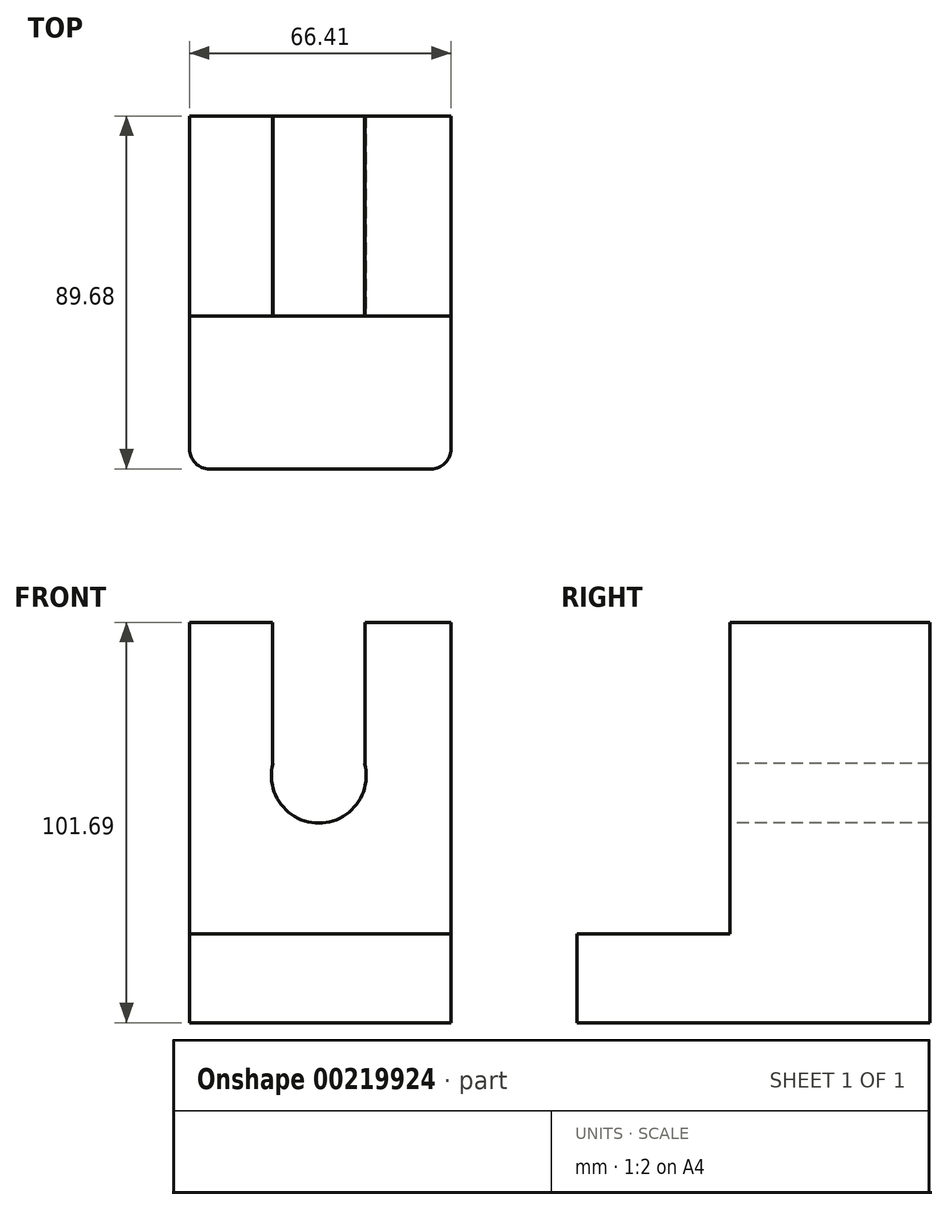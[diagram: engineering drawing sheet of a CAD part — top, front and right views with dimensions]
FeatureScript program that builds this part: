
annotation { "Feature Type Name" : "Feature", "Feature Type Description" : "" }
export const myFeature = defineFeature(function(context is Context, id is Id, definition is map)
    precondition{}
    {
        {
            var Q0;
            Q0=qCreatedBy(makeId("Front.planeOp"),FACE);
            var sketch = newSketch(context, id + "F0", { "sketchPlane" : qUnion([Q0])});
            skLineSegment(sketch, "E0", {"start": v(-33.08, 56) * mm, "end": v(33.33, 56) * mm});
            skLineSegment(sketch, "E1", {"start": v(33.33, 56) * mm, "end": v(33.33, -45.7) * mm});
            skLineSegment(sketch, "E2", {"start": v(-33.08, 56) * mm, "end": v(-33.08, -45.7) * mm});
            skLineSegment(sketch, "E3", {"start": v(-33.08, -45.7) * mm, "end": v(33.33, -45.7) * mm});
            skSolve(sketch);
        }
        {
            var Q0;
            Q0 = qSketchRegion(id + "F0", true);
            extrude(context, id + "F1", {"entities" : qUnion([Q0]), "depth" : 50.8 * mm});
        }
        {
            var Q0;
            Q0=makeQuery(id+"F1.opExtrude","CAP_FACE",FACE,{"disambiguationData":[OSD([sQuery(id+"F0.wireOp",EDGE,"E0"),sQuery(id+"F0.wireOp",EDGE,"E1"),sQuery(id+"F0.wireOp",EDGE,"E2"),sQuery(id+"F0.wireOp",EDGE,"E3")])],"isStart":true});
            var sketch = newSketch(context, id + "F2", { "sketchPlane" : qUnion([Q0])});
            skLineSegment(sketch, "E4", {"start": v(-11.52, 56) * mm, "end": v(-11.52, 20.22) * mm});
            skLineSegment(sketch, "E5", {"start": v(-11.52, 20.22) * mm, "end": v(12, 20.22) * mm});
            skLineSegment(sketch, "E6", {"start": v(12, 20.22) * mm, "end": v(12, 56) * mm});
            skLineSegment(sketch, "E7", {"start": v(12, 56) * mm, "end": v(-11.52, 56) * mm});
            skSolve(sketch);
        }
        {
            var Q0;
            Q0=makeQuery(id+"F2.imprint","IMPRINT",FACE,{"disambiguationData":[TD([[makeQuery(id+"F2.imprint","IMPRINT",EDGE,{"derivedFrom":sQuery(id+"F2.wireOp",EDGE,"E4")}),1.0]])]});
            extrude(context, id + "F3", {"entities" : qUnion([Q0]), "operationType" : NewBodyOperationType.REMOVE, "oppositeDirection" : true, "depth" : 78.23 * mm});
        }
        {
            var Q0;
            Q0=makeQuery(id+"F1.opExtrude","CAP_FACE",FACE,{"disambiguationData":[OSD([sQuery(id+"F0.wireOp",EDGE,"E0"),sQuery(id+"F0.wireOp",EDGE,"E1"),sQuery(id+"F0.wireOp",EDGE,"E2"),sQuery(id+"F0.wireOp",EDGE,"E3")])],"isStart":false});
            var sketch = newSketch(context, id + "F4", { "sketchPlane" : qUnion([Q0])});
            skCircle(sketch, "E8", {"center": v(-0.25, 17.03) * mm, "radius": 12.03 * mm});
            skPoint(sketch, "E8.centerSnap0", {"position": v(-0.25, 20.22) * mm});
            skSolve(sketch);
        }
        {
            var Q0;
            Q0 = qSketchRegion(id + "F4", true);
            extrude(context, id + "F5", {"entities" : qUnion([Q0]), "operationType" : NewBodyOperationType.REMOVE, "oppositeDirection" : true, "depth" : 92.2 * mm});
        }
        {
            var Q0;
            Q0=makeQuery(id+"F1.opExtrude","SWEPT_FACE",FACE,{"disambiguationData":[OSD([sQuery(id+"F0.wireOp",EDGE,"E3")])]});
            var sketch = newSketch(context, id + "F6", { "sketchPlane" : qUnion([Q0])});
            skLineSegment(sketch, "E9", {"start": v(33.33, 50.8) * mm, "end": v(33.33, 89.68) * mm});
            skLineSegment(sketch, "E10", {"start": v(-33.08, 50.8) * mm, "end": v(-33.08, 89.68) * mm});
            skLineSegment(sketch, "E11", {"start": v(-33.08, 89.68) * mm, "end": v(33.33, 89.68) * mm});
            skSolve(sketch);
        }
        {
            var Q0;
            Q0 = qSketchRegion(id + "F6", true);
            var Q1;
            Q1=makeQuery(id+"F6.imprint","IMPRINT",FACE,{"disambiguationData":[TD([[makeQuery(id+"F6.imprint","IMPRINT",EDGE,{"derivedFrom":sQuery(id+"F6.wireOp",EDGE,"E9")}),1.0]])]});
            extrude(context, id + "F7", {"entities" : qUnion([Q0, Q1]), "operationType" : NewBodyOperationType.ADD, "oppositeDirection" : true, "depth" : 22.6 * mm});
        }
        {
            var Q0;
            Q0=makeQuery(id+"F7.opExtrude","SWEPT_EDGE",EDGE,{"disambiguationData":[OSD([sQuery(id+"F6.wireOp",EDGE,"E9"),sQuery(id+"F6.wireOp",EDGE,"E11")])]});
            var Q1;
            Q1=makeQuery(id+"F7.opExtrude","SWEPT_EDGE",EDGE,{"disambiguationData":[OSD([sQuery(id+"F6.wireOp",EDGE,"E10"),sQuery(id+"F6.wireOp",EDGE,"E11")])]});
            fillet(context, id + "F8", {"entities" : qUnion([Q0, Q1]), "radius" : 5.08 * mm, "tangentPropagation" : true, "allowEdgeOverflow" : false});
        }
    });
